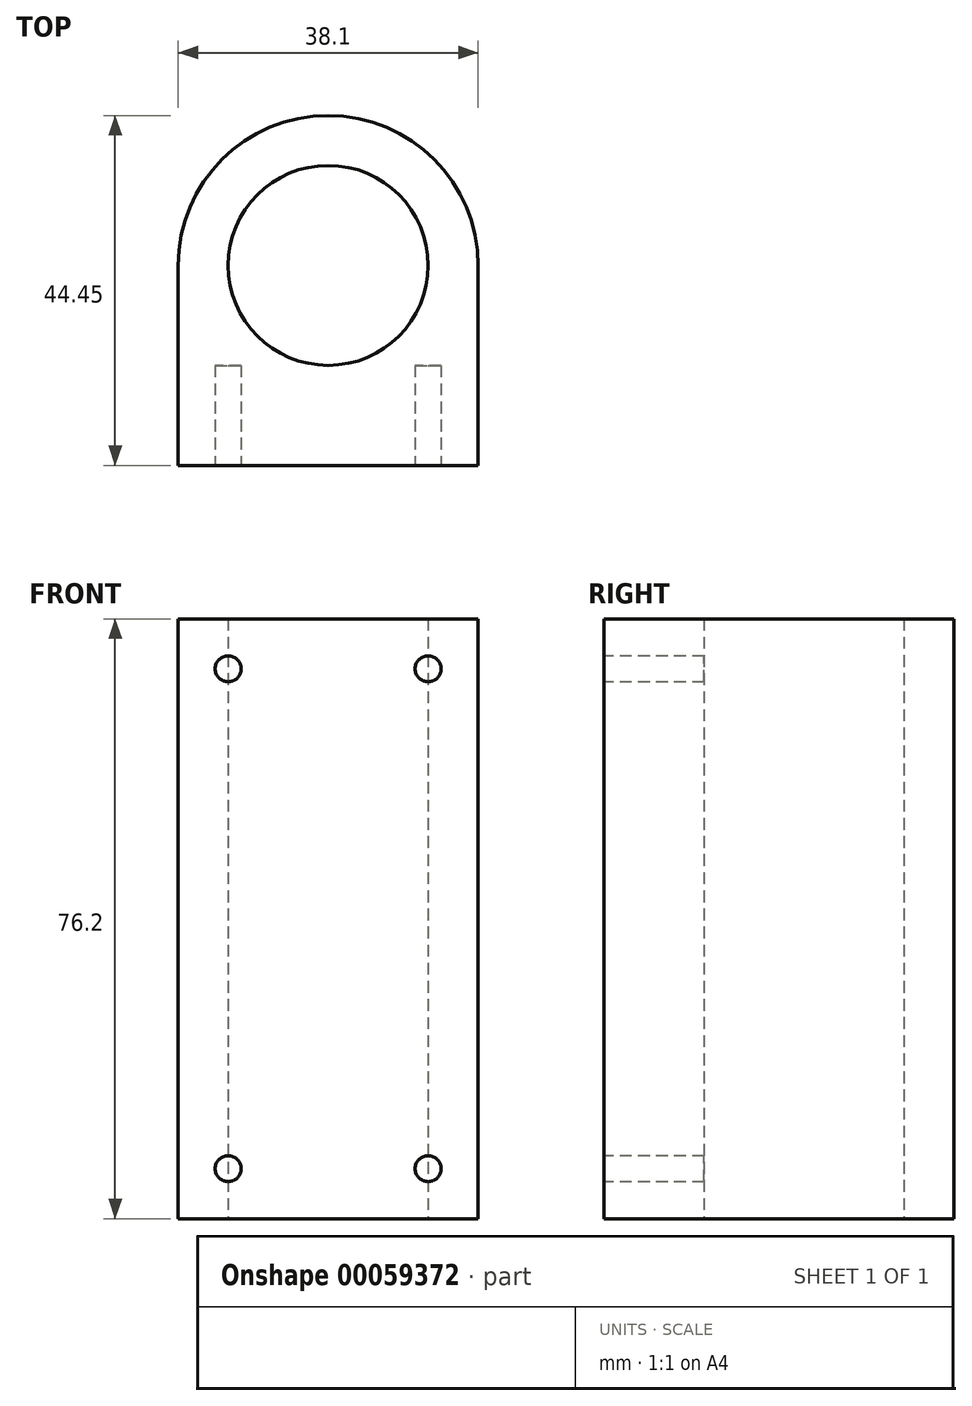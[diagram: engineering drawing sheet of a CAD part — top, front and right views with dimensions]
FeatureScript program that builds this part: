
annotation { "Feature Type Name" : "Feature", "Feature Type Description" : "" }
export const myFeature = defineFeature(function(context is Context, id is Id, definition is map)
    precondition{}
    {
        {
            var Q0;
            Q0=qCreatedBy(makeId("Top.planeOp"),FACE);
            var sketch = newSketch(context, id + "F0", { "sketchPlane" : qUnion([Q0])});
            skCircle(sketch, "E0", {"center": v(0, 0) * mm, "radius": 12.7 * mm});
            skArc(sketch, "E1", {"start": v(19.05, 0) * mm, "mid": v(0, 19.05) * mm, "end": v(-19.05, 0) * mm});
            skLineSegment(sketch, "E2", {"start": v(-19.05, 0) * mm, "end": v(-19.05, -25.4) * mm});
            skLineSegment(sketch, "E3", {"start": v(-19.05, -25.4) * mm, "end": v(19.05, -25.4) * mm});
            skLineSegment(sketch, "E4", {"start": v(19.05, -25.4) * mm, "end": v(19.05, 0) * mm});
            skSolve(sketch);
        }
        {
            var Q0;
            Q0=makeQuery(id+"F0.imprint","IMPRINT",FACE,{"disambiguationData":[TD([[makeQuery(id+"F0.imprint","IMPRINT",EDGE,{"derivedFrom":sQuery(id+"F0.wireOp",EDGE,"E0")}),-1.0]])]});
            extrude(context, id + "F1", {"entities" : qUnion([Q0]), "endBound" : BoundingType.SYMMETRIC, "depth" : 76.2 * mm});
        }
        {
            var Q0;
            Q0=makeQuery(id+"F1.opExtrude","SWEPT_FACE",FACE,{"disambiguationData":[OSD([sQuery(id+"F0.wireOp",EDGE,"E3")])]});
            var sketch = newSketch(context, id + "F2", { "sketchPlane" : qUnion([Q0])});
            skLineSegment(sketch, "E5.0", {"start": v(-19.05, -31.75) * mm, "end": v(-14.35, -31.75) * mm});
            skLineSegment(sketch, "E6.0", {"start": v(-12.7, 38.1) * mm, "end": v(-12.7, 33.4) * mm});
            skLineSegment(sketch, "E7.0", {"start": v(-19.05, 31.75) * mm, "end": v(-14.35, 31.75) * mm});
            skLineSegment(sketch, "E8.0", {"start": v(12.7, 38.1) * mm, "end": v(12.7, 33.4) * mm});
            skCircle(sketch, "E9", {"center": v(-12.7, -31.75) * mm, "radius": 1.65 * mm});
            skCircle(sketch, "E10", {"center": v(12.7, -31.75) * mm, "radius": 1.65 * mm});
            skCircle(sketch, "E11", {"center": v(-12.7, 31.75) * mm, "radius": 1.65 * mm});
            skCircle(sketch, "E12", {"center": v(12.7, 31.75) * mm, "radius": 1.65 * mm});
            skLineSegment(sketch, "E13.trimOffspring", {"start": v(-12.7, -33.4) * mm, "end": v(-12.7, -38.1) * mm});
            skLineSegment(sketch, "E14.trimOffspring", {"start": v(-11.05, -31.75) * mm, "end": v(11.05, -31.75) * mm});
            skLineSegment(sketch, "E15.trimOffspring", {"start": v(14.35, -31.75) * mm, "end": v(19.05, -31.75) * mm});
            skLineSegment(sketch, "E16.trimOffspring", {"start": v(12.7, -33.4) * mm, "end": v(12.7, -38.1) * mm});
            skLineSegment(sketch, "E17.trimOffspring", {"start": v(-12.7, 30.1) * mm, "end": v(-12.7, -30.1) * mm});
            skLineSegment(sketch, "E18.trimOffspring", {"start": v(-11.05, 31.75) * mm, "end": v(11.05, 31.75) * mm});
            skLineSegment(sketch, "E19.trimOffspring", {"start": v(14.35, 31.75) * mm, "end": v(19.05, 31.75) * mm});
            skLineSegment(sketch, "E20.trimOffspring", {"start": v(12.7, 30.1) * mm, "end": v(12.7, -30.1) * mm});
            skSolve(sketch);
        }
        {
            var Q0;
            {var subQ0=sQuery(id+"F2.wireOp",EDGE,"E9");var subQ1=makeQuery(id+"F2.imprint","INTERSECT",VERTEX,{"derivedFrom":[subQ0,sQuery(id+"F2.wireOp",EDGE,"E14.trimOffspring")]});Q0=makeQuery(id+"F2.imprint","IMPRINT",FACE,{"disambiguationData":[TD([[makeQuery(id+"F2.imprint","IMPRINT",EDGE,{"disambiguationData":[TD([[subQ1,-1.0]])],"derivedFrom":subQ0}),1.0]])]});}
            var Q1;
            {var subQ0=sQuery(id+"F2.wireOp",EDGE,"E10");var subQ1=makeQuery(id+"F2.imprint","INTERSECT",VERTEX,{"derivedFrom":[subQ0,sQuery(id+"F2.wireOp",EDGE,"E15.trimOffspring")]});Q1=makeQuery(id+"F2.imprint","IMPRINT",FACE,{"disambiguationData":[TD([[makeQuery(id+"F2.imprint","IMPRINT",EDGE,{"disambiguationData":[TD([[subQ1,-1.0]])],"derivedFrom":subQ0}),1.0]])]});}
            var Q2;
            {var subQ0=sQuery(id+"F2.wireOp",EDGE,"E11");var subQ1=makeQuery(id+"F2.imprint","INTERSECT",VERTEX,{"derivedFrom":[sQuery(id+"F2.wireOp",EDGE,"E6.0"),subQ0]});Q2=makeQuery(id+"F2.imprint","IMPRINT",FACE,{"disambiguationData":[TD([[makeQuery(id+"F2.imprint","IMPRINT",EDGE,{"disambiguationData":[TD([[subQ1,1.0]])],"derivedFrom":subQ0}),1.0]])]});}
            var Q3;
            {var subQ0=sQuery(id+"F2.wireOp",EDGE,"E12");var subQ1=makeQuery(id+"F2.imprint","INTERSECT",VERTEX,{"derivedFrom":[sQuery(id+"F2.wireOp",EDGE,"E8.0"),subQ0]});Q3=makeQuery(id+"F2.imprint","IMPRINT",FACE,{"disambiguationData":[TD([[makeQuery(id+"F2.imprint","IMPRINT",EDGE,{"disambiguationData":[TD([[subQ1,1.0]])],"derivedFrom":subQ0}),1.0]])]});}
            extrude(context, id + "F3", {"entities" : qUnion([Q0, Q1, Q2, Q3]), "operationType" : NewBodyOperationType.REMOVE, "oppositeDirection" : true, "depth" : 12.7 * mm});
        }
    });
